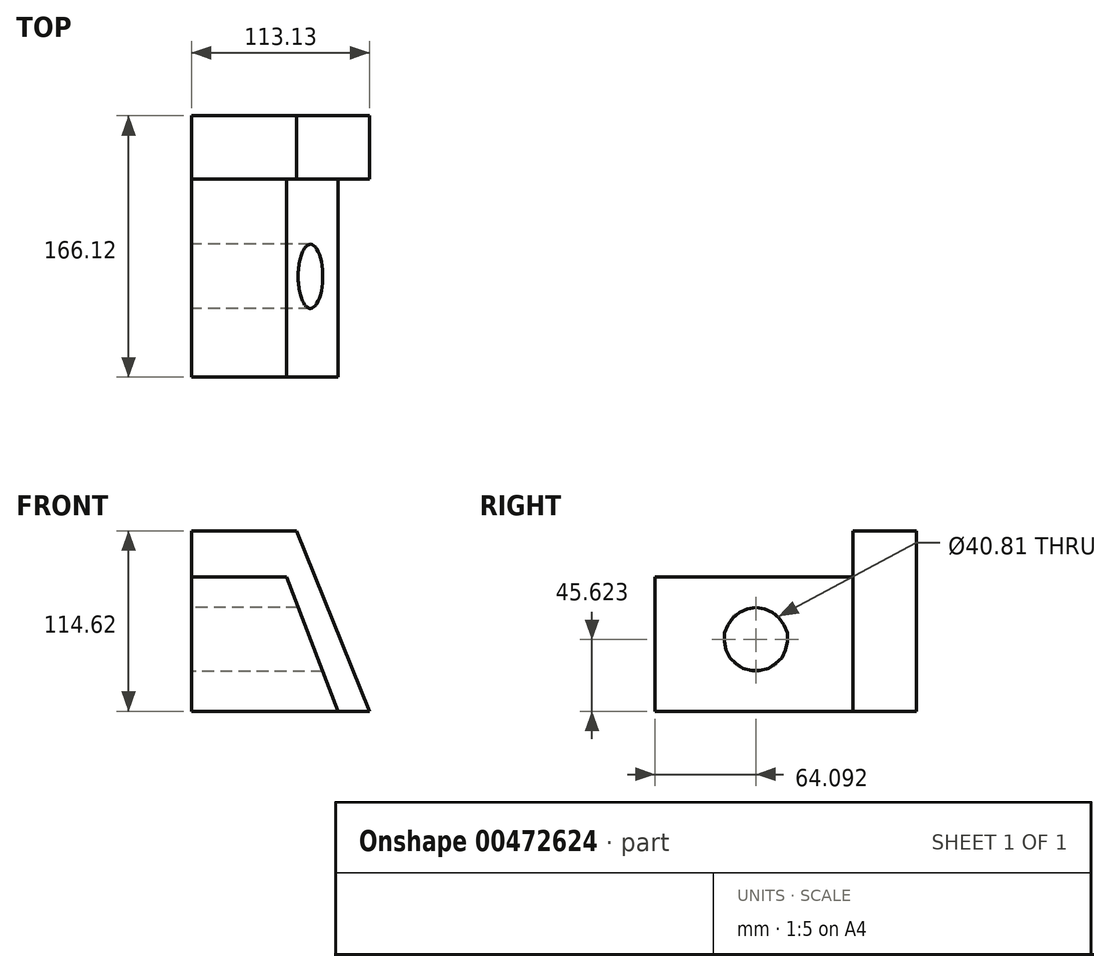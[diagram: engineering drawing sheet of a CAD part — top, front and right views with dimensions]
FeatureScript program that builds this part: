
annotation { "Feature Type Name" : "Feature", "Feature Type Description" : "" }
export const myFeature = defineFeature(function(context is Context, id is Id, definition is map)
    precondition{}
    {
        {
            var Q0;
            Q0=qCreatedBy(makeId("Front.planeOp"),FACE);
            var sketch = newSketch(context, id + "F0", { "sketchPlane" : qUnion([Q0])});
            skLineSegment(sketch, "E0", {"start": v(-49.92, -60.2) * mm, "end": v(-49.92, 54.42) * mm});
            skLineSegment(sketch, "E1", {"start": v(-49.92, 54.42) * mm, "end": v(16.88, 54.42) * mm});
            skLineSegment(sketch, "E2", {"start": v(-49.92, -60.2) * mm, "end": v(63.2, -60.2) * mm});
            skLineSegment(sketch, "E3", {"start": v(63.2, -60.2) * mm, "end": v(16.88, 54.42) * mm});
            skSolve(sketch);
        }
        {
            var Q0;
            Q0=makeQuery(id+"F0.imprint","IMPRINT",FACE,{"disambiguationData":[TD([[makeQuery(id+"F0.imprint","IMPRINT",EDGE,{"derivedFrom":sQuery(id+"F0.wireOp",EDGE,"E0")}),-1.0]])]});
            extrude(context, id + "F1", {"entities" : qUnion([Q0]), "depth" : 40.4 * mm});
        }
        {
            var Q0;
            Q0=makeQuery(id+"F1.opExtrude","CAP_FACE",FACE,{"disambiguationData":[OSD([sQuery(id+"F0.wireOp",EDGE,"E0"),sQuery(id+"F0.wireOp",EDGE,"E1"),sQuery(id+"F0.wireOp",EDGE,"E2"),sQuery(id+"F0.wireOp",EDGE,"E3")])],"isStart":false});
            var sketch = newSketch(context, id + "F2", { "sketchPlane" : qUnion([Q0])});
            skLineSegment(sketch, "E4", {"start": v(-49.92, -60.2) * mm, "end": v(-49.92, 24.99) * mm});
            skLineSegment(sketch, "E5", {"start": v(-49.92, 24.99) * mm, "end": v(10.39, 24.99) * mm});
            skLineSegment(sketch, "E6", {"start": v(10.39, 24.99) * mm, "end": v(43.07, -60.2) * mm});
            skSolve(sketch);
        }
        {
            var Q0;
            {var subQ0=sQuery(id+"F2.wireOp",EDGE,"E4");Q0=makeQuery(id+"F2.imprint","IMPRINT",FACE,{"disambiguationData":[TD([[makeQuery(id+"F2.imprint","IMPRINT",EDGE,{"derivedFrom":subQ0}),-1.0]])]});}
            extrude(context, id + "F3", {"entities" : qUnion([Q0]), "operationType" : NewBodyOperationType.ADD, "depth" : 125.73 * mm});
        }
        {
            var Q0;
            Q0=makeQuery(id+"F3.boolean.opBoolean","MERGE",FACE,{"derivedFrom":[makeQuery(id+"F1.opExtrude","SWEPT_FACE",FACE,{"disambiguationData":[OSD([sQuery(id+"F0.wireOp",EDGE,"E0")])]}),makeQuery(id+"F3.opExtrude","SWEPT_FACE",FACE,{"disambiguationData":[OSD([sQuery(id+"F2.wireOp",EDGE,"E4")])]})]});
            var sketch = newSketch(context, id + "F4", { "sketchPlane" : qUnion([Q0])});
            skCircle(sketch, "E7", {"center": v(102.03, -14.58) * mm, "radius": 20.4 * mm});
            skSolve(sketch);
        }
        {
            var Q0;
            Q0=makeQuery(id+"F4.imprint","IMPRINT",FACE,{"disambiguationData":[TD([[makeQuery(id+"F4.imprint","IMPRINT",EDGE,{"derivedFrom":sQuery(id+"F4.wireOp",EDGE,"E7")}),1.0]])]});
            extrude(context, id + "F5", {"entities" : qUnion([Q0]), "operationType" : NewBodyOperationType.REMOVE, "oppositeDirection" : true, "depth" : 136.65 * mm});
        }
    });
